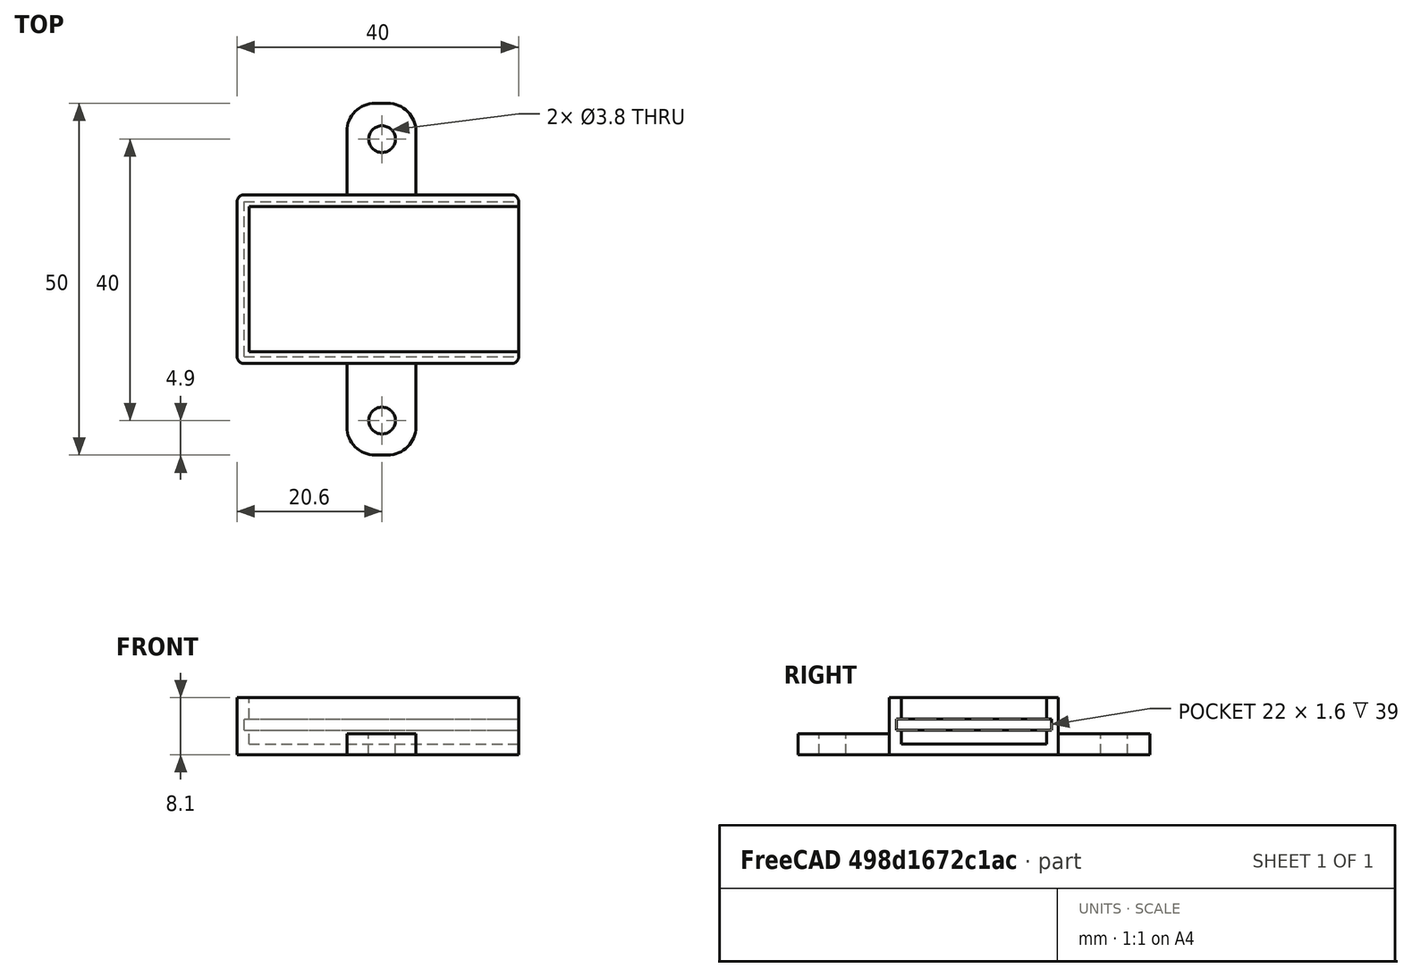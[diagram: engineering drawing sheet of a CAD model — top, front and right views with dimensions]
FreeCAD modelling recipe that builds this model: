
FCSTD DOCUMENT  (FreeCAD 0.18.4R)
Label: pcb_pl2303
License: FreeArt
LicenseURL: http://artlibre.org/licence/lal
objects: Part::Box×4, Part::Fillet×2, Part::Cut×2, Part::MultiFuse×2, Spreadsheet::Sheet×1, Part::Cylinder×1, Part::FeaturePython×1, App::Part×1
note: 12 computed .brp shape members not serialized (recipe doc carries the construction recipe); baked Part::Feature solids carry a one-line shape summary decoded from their .brp

FEATURE [Spreadsheet::Sheet] Spreadsheet  label="p"
  cells = A1=pcb_x; B1(pcb_x)=39; A2=pcb_y; B2(pcb_y)=22; A3=pcb_z; B3(pcb_z)=1.6; A4=pcb_under; B4(pcb_under)=2; A5=side_wall; B5(side_wall)=1; A6=attach_hole_dist; B6(attach_hole_dist)=10; A7=attach_hole_r; B7(attach_hole_r)=1.9; A8=attach_hole_wall; B8(attach_hole_wall)=3; A9=attach_z; B9(attach_z)=3; A10=pcb_side_lane; B10(pcb_side_lane)=0.7; A11=bottom_wall; B11(bottom_wall)=1.5; A12=pcb_above; B12(pcb_above)=3
FEATURE [Part::Box] Box005  label="ears cube"
  AttacherType = Attacher::AttachEngine3D
  Height = 3
  Length = 9.8
  Width = 50
  expr: Height = p.attach_z
  expr: Length = (p.attach_hole_r + p.attach_hole_wall) * 2
  expr: Width = floor((p.pcb_y + 2 * p.side_wall) / p.attach_hole_dist + 3) * p.attach_hole_dist
FEATURE [Part::Fillet] Fillet002  label="ears cube fillet"
  Base = -> Box005
  Edges = 4 edges r=4: [Edge1,Edge3,Edge5,Edge7]
FEATURE [Part::Cylinder] Cylinder001  label="attach hole"
  Angle = 360
  AttacherType = Attacher::AttachEngine3D
  Height = 10
  Placement = pos=(5,4.9,0) rot=(0,0,1;0rad)
  Radius = 1.9
  expr: Placement.Base.x = p.attach_hole_dist / 2
  expr: Placement.Base.y = p.attach_hole_r + p.attach_hole_wall
  expr: Radius = p.attach_hole_r
FEATURE [Part::FeaturePython] Array002  label="attach hole array"  # Draft array (typed FeaturePython)
  Angle = 360
  ArrayType = 0
  Axis = (0,0,1)
  Base = -> Cylinder001
  Center = (0,0,0)
  Fuse = false
  IntervalAxis = (0,0,0)
  IntervalX = (1,0,0)
  IntervalY = (0,40,0)
  IntervalZ = (0,0,1)
  NumberPolar = 1
  NumberX = 1
  NumberY = 2
  NumberZ = 1
  expr: IntervalY.y = floor((p.pcb_y + 2 * p.side_wall) / p.attach_hole_dist + 2) * p.attach_hole_dist
FEATURE [Part::Cut] Cut002  label="attach plane"
  Base = -> Fillet002
  Placement = pos=(15.6,-13,0) rot=(0,0,1;0rad)
  Tool = -> Array002
  expr: Placement.Base.y = -(floor(p.pcb_y / p.attach_hole_dist + 3) * p.attach_hole_dist - p.side_wall * 2 - p.pcb_y) / 2
  expr: Placement.Base.x = p.side_wall + p.pcb_x / 2 - (p.attach_hole_r + p.attach_hole_wall)
FEATURE [Part::Box] Box  label="external cube"
  AttacherType = Attacher::AttachEngine3D
  Height = 8.1
  Length = 40
  Width = 24
  expr: Height = p.bottom_wall + p.pcb_under + p.pcb_z + p.pcb_above
  expr: Width = p.pcb_y + 2 * p.side_wall
  expr: Length = p.pcb_x + p.side_wall
FEATURE [Part::Box] Box006  label="internal cube"
  AttacherType = Attacher::AttachEngine3D
  Height = 6.6
  Length = 38.6
  Placement = pos=(1.7,1.7,1.5) rot=(0,0,1;0rad)
  Width = 20.6
  expr: Placement.Base.y = p.side_wall + p.pcb_side_lane
  expr: Placement.Base.x = p.side_wall + p.pcb_side_lane
  expr: Placement.Base.z = p.bottom_wall
  expr: Height = p.pcb_under + p.pcb_z + p.pcb_above
  expr: Width = p.pcb_y - 2 * p.pcb_side_lane
  expr: Length = p.pcb_x - 2 * p.pcb_side_lane + p.side_wall
FEATURE [Part::Box] Box007  label="pcb extract cube"
  AttacherType = Attacher::AttachEngine3D
  Height = 1.6
  Length = 39
  Placement = pos=(1,1,3.5) rot=(0,0,1;0rad)
  Width = 22
  expr: Placement.Base.y = p.side_wall
  expr: Placement.Base.x = p.side_wall
  expr: Length = p.pcb_x
  expr: Width = p.pcb_y
  expr: Placement.Base.z = p.bottom_wall + p.pcb_under
  expr: Height = p.pcb_z
FEATURE [Part::MultiFuse] Fusion  label="extract fusion"
  Shapes = -> [Box006,Box007]
FEATURE [Part::Fillet] Fillet  label="external fillet"
  Base = -> Box
  Edges = 4 edges r=1: [Edge1,Edge3,Edge5,Edge7]
FEATURE [Part::MultiFuse] Fusion001  label="pl2303 fusion"
  Shapes = -> [Cut002,Fillet]
FEATURE [Part::Cut] Cut  label="pl2303 cut"
  Base = -> Fusion001
  Tool = -> Fusion
FEATURE [App::Part] Part  label="pl2303 pcb box part"
  Group = -> [Box005,Fillet002,Box,Cut002,Fillet,Fusion001,Fusion,Box007,Box006,Array002,Cylinder001,Cut]
  Origin = -> Origin
